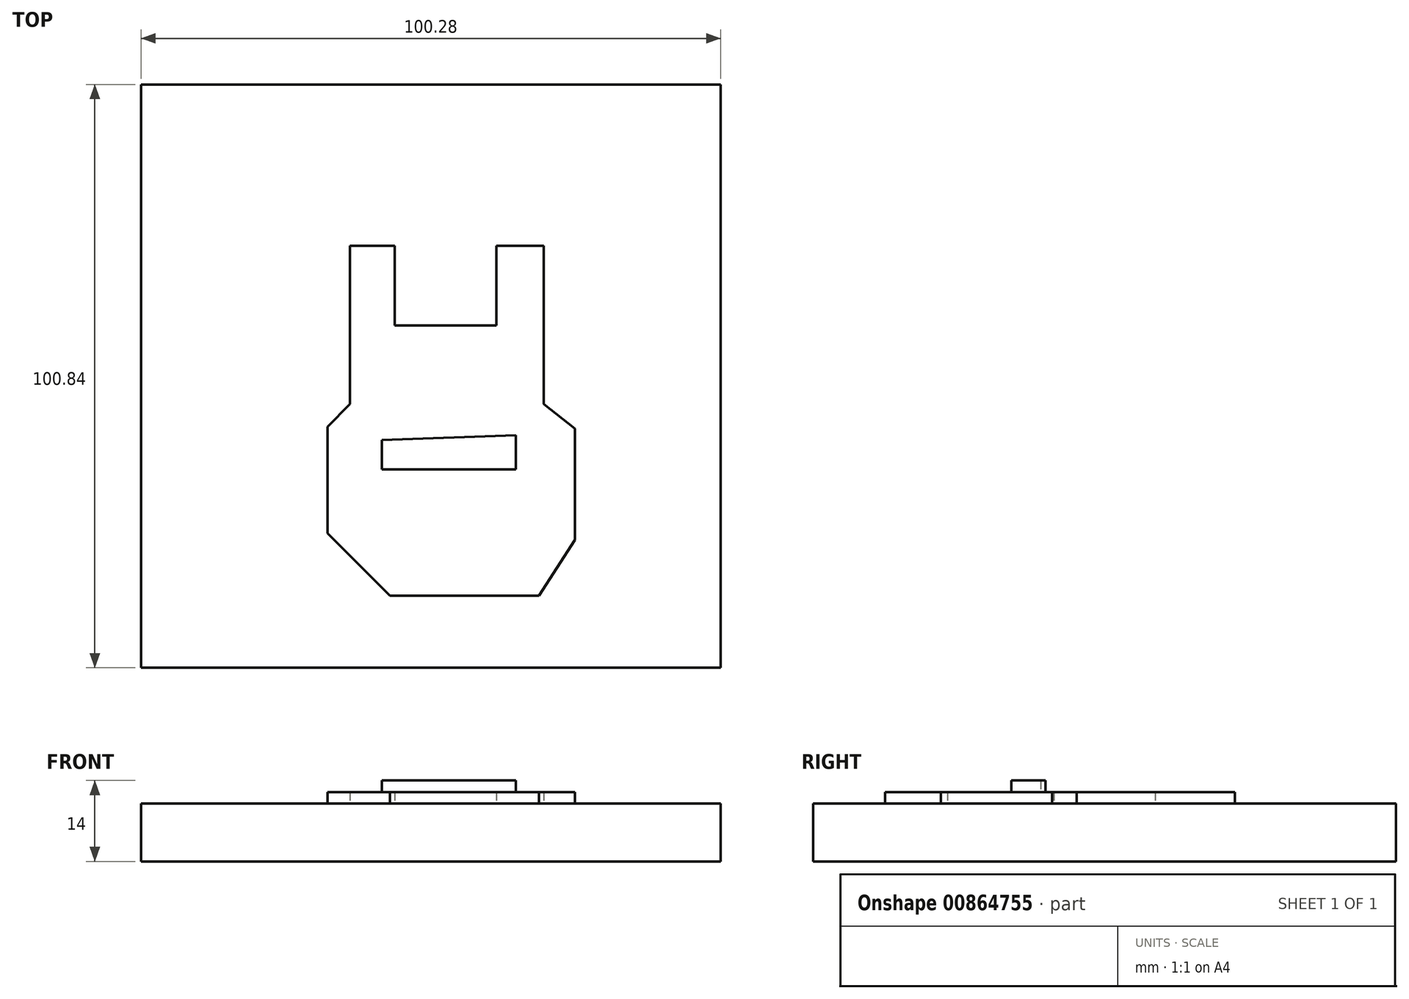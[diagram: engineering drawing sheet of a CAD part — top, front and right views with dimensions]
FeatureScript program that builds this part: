
annotation { "Feature Type Name" : "Feature", "Feature Type Description" : "" }
export const myFeature = defineFeature(function(context is Context, id is Id, definition is map)
    precondition{}
    {
        {
            var Q0;
            Q0=qCreatedBy(makeId("Top.planeOp"),FACE);
            var sketch = newSketch(context, id + "F0", { "sketchPlane" : qUnion([Q0])});
            skLineSegment(sketch, "E0.bottom", {"start": v(-36.12, 27.9) * mm, "end": v(64.16, 27.9) * mm});
            skLineSegment(sketch, "E0.top", {"start": v(-36.12, -72.94) * mm, "end": v(64.16, -72.94) * mm});
            skLineSegment(sketch, "E0.left", {"start": v(-36.12, 27.9) * mm, "end": v(-36.12, -72.94) * mm});
            skLineSegment(sketch, "E0.right", {"start": v(64.16, 27.9) * mm, "end": v(64.16, -72.94) * mm});
            skSolve(sketch);
        }
        {
            var Q0;
            Q0=makeQuery(id+"F0.imprint","IMPRINT",FACE,{"disambiguationData":[TD([[makeQuery(id+"F0.imprint","IMPRINT",EDGE,{"derivedFrom":sQuery(id+"F0.wireOp",EDGE,"E0.bottom")}),-1.0]])]});
            extrude(context, id + "F1", {"entities" : qUnion([Q0]), "depth" : 10 * mm, "offsetDistance" : 25 * mm});
        }
        {
            var Q0;
            Q0=makeQuery(id+"F1.opExtrude","CAP_FACE",FACE,{"disambiguationData":[OSD([sQuery(id+"F0.wireOp",EDGE,"E0.bottom"),sQuery(id+"F0.wireOp",EDGE,"E0.top"),sQuery(id+"F0.wireOp",EDGE,"E0.left"),sQuery(id+"F0.wireOp",EDGE,"E0.right")])],"isStart":false});
            var sketch = newSketch(context, id + "F2", { "sketchPlane" : qUnion([Q0])});
            skLineSegment(sketch, "E1", {"start": v(0, 0) * mm, "end": v(0, -27.34) * mm});
            skLineSegment(sketch, "E2", {"start": v(0, -27.34) * mm, "end": v(-3.82, -31.3) * mm});
            skLineSegment(sketch, "E3", {"start": v(-3.82, -31.3) * mm, "end": v(-3.82, -49.71) * mm});
            skLineSegment(sketch, "E4", {"start": v(-3.82, -49.71) * mm, "end": v(6.94, -60.48) * mm});
            skLineSegment(sketch, "E5", {"start": v(6.94, -60.48) * mm, "end": v(32.72, -60.48) * mm});
            skLineSegment(sketch, "E6", {"start": v(32.72, -60.48) * mm, "end": v(38.95, -50.85) * mm});
            skLineSegment(sketch, "E7", {"start": v(38.95, -50.85) * mm, "end": v(38.95, -31.58) * mm});
            skLineSegment(sketch, "E8", {"start": v(38.95, -31.58) * mm, "end": v(33.57, -27.34) * mm});
            skLineSegment(sketch, "E9", {"start": v(33.57, -27.34) * mm, "end": v(33.57, 0) * mm});
            skLineSegment(sketch, "E10", {"start": v(33.57, 0) * mm, "end": v(25.35, 0) * mm});
            skLineSegment(sketch, "E11", {"start": v(25.35, 0) * mm, "end": v(25.35, -13.74) * mm});
            skLineSegment(sketch, "E12", {"start": v(25.35, -13.74) * mm, "end": v(7.8, -13.74) * mm});
            skLineSegment(sketch, "E13", {"start": v(7.8, -13.74) * mm, "end": v(7.8, 0) * mm});
            skLineSegment(sketch, "E14", {"start": v(7.8, 0) * mm, "end": v(0, 0) * mm});
            skSolve(sketch);
        }
        {
            var Q0;
            Q0=makeQuery(id+"F2.imprint","IMPRINT",FACE,{"disambiguationData":[TD([[makeQuery(id+"F2.imprint","IMPRINT",EDGE,{"derivedFrom":sQuery(id+"F2.wireOp",EDGE,"E1")}),1.0]])]});
            extrude(context, id + "F3", {"entities" : qUnion([Q0]), "operationType" : NewBodyOperationType.ADD, "depth" : 2 * mm, "offsetDistance" : 25 * mm});
        }
        {
            var Q0;
            Q0=makeQuery(id+"F3.opExtrude","CAP_FACE",FACE,{"disambiguationData":[OSD([sQuery(id+"F2.wireOp",EDGE,"E1"),sQuery(id+"F2.wireOp",EDGE,"E2"),sQuery(id+"F2.wireOp",EDGE,"E3"),sQuery(id+"F2.wireOp",EDGE,"E4"),sQuery(id+"F2.wireOp",EDGE,"E5"),sQuery(id+"F2.wireOp",EDGE,"E6"),sQuery(id+"F2.wireOp",EDGE,"E7"),sQuery(id+"F2.wireOp",EDGE,"E8"),sQuery(id+"F2.wireOp",EDGE,"E9"),sQuery(id+"F2.wireOp",EDGE,"E10"),sQuery(id+"F2.wireOp",EDGE,"E11"),sQuery(id+"F2.wireOp",EDGE,"E12"),sQuery(id+"F2.wireOp",EDGE,"E13"),sQuery(id+"F2.wireOp",EDGE,"E14")])],"isStart":false});
            var sketch = newSketch(context, id + "F4", { "sketchPlane" : qUnion([Q0])});
            skLineSegment(sketch, "E15", {"start": v(7.8, -35.83) * mm, "end": v(28.19, -35.83) * mm});
            skLineSegment(sketch, "E16", {"start": v(28.19, -35.83) * mm, "end": v(28.19, -39.52) * mm});
            skLineSegment(sketch, "E17", {"start": v(28.19, -39.52) * mm, "end": v(7.8, -39.52) * mm});
            skLineSegment(sketch, "E18", {"start": v(7.8, -39.52) * mm, "end": v(7.8, -35.83) * mm});
            skSolve(sketch);
        }
        {
            var Q0;
            Q0=makeQuery(id+"F4.imprint","IMPRINT",FACE,{"disambiguationData":[TD([[makeQuery(id+"F4.imprint","IMPRINT",EDGE,{"derivedFrom":sQuery(id+"F4.wireOp",EDGE,"E15")}),-1.0]])]});
            extrude(context, id + "F5", {"entities" : qUnion([Q0]), "operationType" : NewBodyOperationType.ADD, "oppositeDirection" : true, "depth" : 2 * mm, "offsetDistance" : 25 * mm});
        }
        {
            var Q0;
            Q0=makeQuery(id+"F3.opExtrude","CAP_FACE",FACE,{"disambiguationData":[OSD([sQuery(id+"F2.wireOp",EDGE,"E1"),sQuery(id+"F2.wireOp",EDGE,"E2"),sQuery(id+"F2.wireOp",EDGE,"E3"),sQuery(id+"F2.wireOp",EDGE,"E4"),sQuery(id+"F2.wireOp",EDGE,"E5"),sQuery(id+"F2.wireOp",EDGE,"E6"),sQuery(id+"F2.wireOp",EDGE,"E7"),sQuery(id+"F2.wireOp",EDGE,"E8"),sQuery(id+"F2.wireOp",EDGE,"E9"),sQuery(id+"F2.wireOp",EDGE,"E10"),sQuery(id+"F2.wireOp",EDGE,"E11"),sQuery(id+"F2.wireOp",EDGE,"E12"),sQuery(id+"F2.wireOp",EDGE,"E13"),sQuery(id+"F2.wireOp",EDGE,"E14")])],"isStart":false});
            var sketch = newSketch(context, id + "F6", { "sketchPlane" : qUnion([Q0])});
            skLineSegment(sketch, "E19", {"start": v(5.52, -33.57) * mm, "end": v(5.52, -38.67) * mm});
            skLineSegment(sketch, "E20", {"start": v(5.52, -38.67) * mm, "end": v(28.75, -38.67) * mm});
            skLineSegment(sketch, "E21", {"start": v(28.75, -38.67) * mm, "end": v(28.75, -32.72) * mm});
            skLineSegment(sketch, "E22", {"start": v(28.75, -32.72) * mm, "end": v(5.52, -33.57) * mm});
            skSolve(sketch);
        }
        {
            var Q0;
            Q0=makeQuery(id+"F6.imprint","IMPRINT",FACE,{"disambiguationData":[TD([[makeQuery(id+"F6.imprint","IMPRINT",EDGE,{"derivedFrom":sQuery(id+"F6.wireOp",EDGE,"E19")}),1.0]])]});
            extrude(context, id + "F7", {"entities" : qUnion([Q0]), "operationType" : NewBodyOperationType.ADD, "depth" : 2 * mm, "offsetDistance" : 25 * mm});
        }
    });
